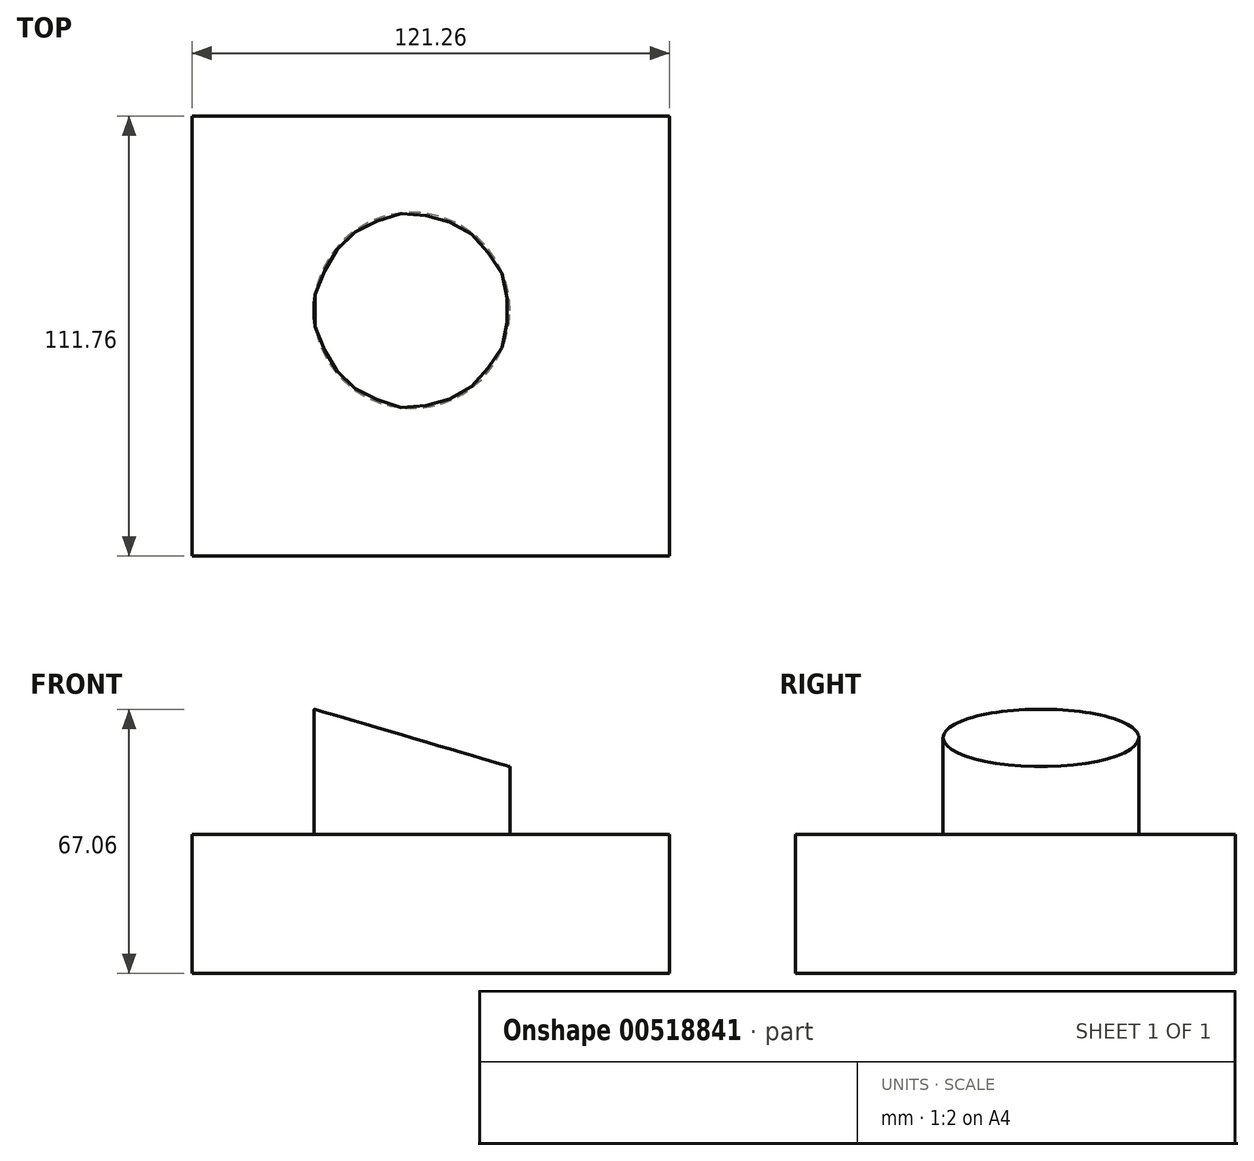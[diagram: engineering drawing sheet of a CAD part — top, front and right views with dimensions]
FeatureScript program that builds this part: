
annotation { "Feature Type Name" : "Feature", "Feature Type Description" : "" }
export const myFeature = defineFeature(function(context is Context, id is Id, definition is map)
    precondition{}
    {
        {
            var Q0;
            Q0=qCreatedBy(makeId("Top.planeOp"),FACE);
            var sketch = newSketch(context, id + "F0", { "sketchPlane" : qUnion([Q0])});
            skLineSegment(sketch, "E0.bottom", {"start": v(-55.82, 49.37) * mm, "end": v(65.44, 49.37) * mm});
            skLineSegment(sketch, "E0.top", {"start": v(-55.82, -62.4) * mm, "end": v(65.44, -62.4) * mm});
            skLineSegment(sketch, "E0.left", {"start": v(-55.82, 49.37) * mm, "end": v(-55.82, -62.4) * mm});
            skLineSegment(sketch, "E0.right", {"start": v(65.44, 49.37) * mm, "end": v(65.44, -62.4) * mm});
            skSolve(sketch);
        }
        {
            var Q0;
            Q0 = qSketchRegion(id + "F0", true);
            extrude(context, id + "F1", {"entities" : qUnion([Q0]), "depth" : 35.3 * mm});
        }
        {
            var Q0;
            Q0=makeQuery(id+"F1.opExtrude","CAP_FACE",FACE,{"disambiguationData":[OSD([sQuery(id+"F0.wireOp",EDGE,"E0.bottom"),sQuery(id+"F0.wireOp",EDGE,"E0.top"),sQuery(id+"F0.wireOp",EDGE,"E0.left"),sQuery(id+"F0.wireOp",EDGE,"E0.right")])],"isStart":false});
            var sketch = newSketch(context, id + "F2", { "sketchPlane" : qUnion([Q0])});
            skCircle(sketch, "E1", {"center": v(0, 0) * mm, "radius": 24.9 * mm});
            skSolve(sketch);
        }
        {
            var Q0;
            Q0 = qSketchRegion(id + "F2", true);
            extrude(context, id + "F3", {"entities" : qUnion([Q0]), "operationType" : NewBodyOperationType.ADD, "depth" : 31.75 * mm});
        }
        {
            var Q0;
            Q0=makeQuery(id+"F1.opExtrude","SWEPT_FACE",FACE,{"disambiguationData":[OSD([sQuery(id+"F0.wireOp",EDGE,"E0.top")])]});
            var sketch = newSketch(context, id + "F4", { "sketchPlane" : qUnion([Q0])});
            skLineSegment(sketch, "E2", {"start": v(-25.69, 67.39) * mm, "end": v(32.4, 50.33) * mm});
            skLineSegment(sketch, "E3", {"start": v(32.4, 50.33) * mm, "end": v(32.4, 79.37) * mm});
            skLineSegment(sketch, "E4", {"start": v(32.4, 79.37) * mm, "end": v(-27.14, 79.37) * mm});
            skLineSegment(sketch, "E5", {"start": v(-27.14, 79.37) * mm, "end": v(-25.69, 67.39) * mm});
            skSolve(sketch);
        }
        {
            var Q0;
            Q0 = qSketchRegion(id + "F4", true);
            extrude(context, id + "F5", {"entities" : qUnion([Q0]), "operationType" : NewBodyOperationType.REMOVE, "oppositeDirection" : true, "depth" : 152.65 * mm});
        }
    });
